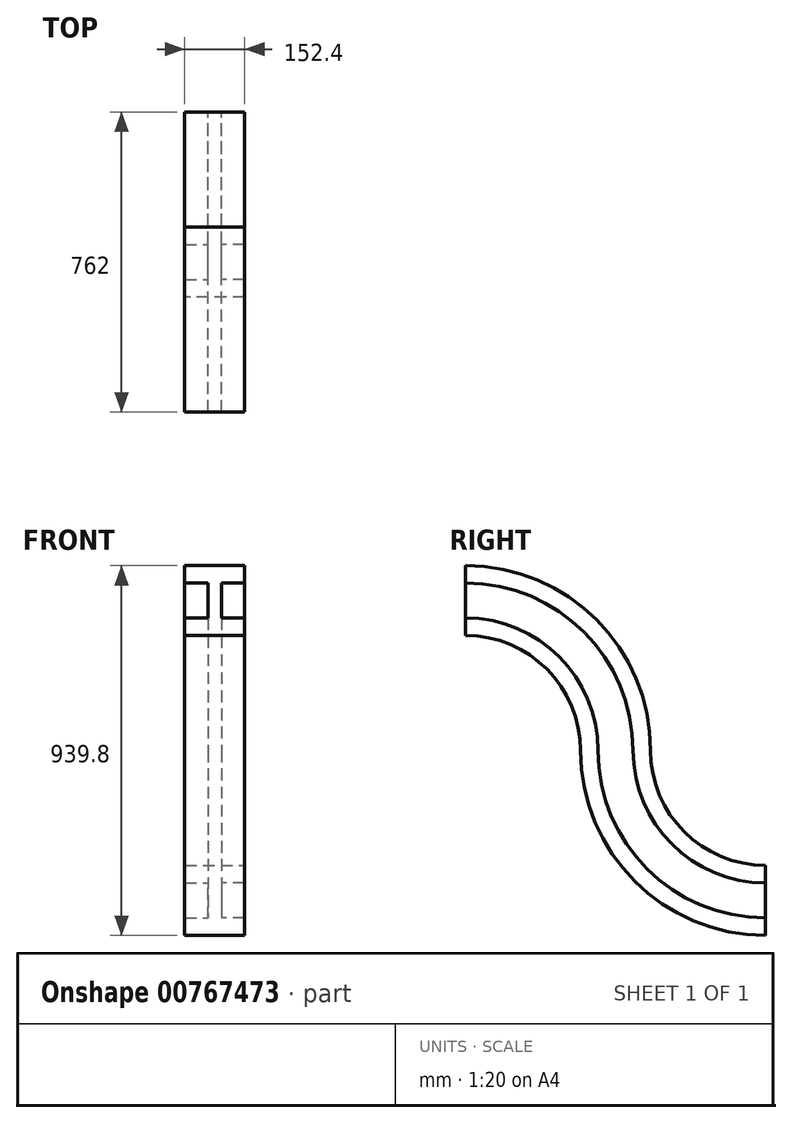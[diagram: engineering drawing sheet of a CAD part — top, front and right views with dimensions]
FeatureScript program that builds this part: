
annotation { "Feature Type Name" : "Feature", "Feature Type Description" : "" }
export const myFeature = defineFeature(function(context is Context, id is Id, definition is map)
    precondition{}
    {
        {
            var Q0;
            Q0=qCreatedBy(makeId("Front.planeOp"),FACE);
            var sketch = newSketch(context, id + "F0", { "sketchPlane" : qUnion([Q0])});
            skLineSegment(sketch, "E0", {"start": v(0, 88.9) * mm, "end": v(76.2, 88.9) * mm});
            skLineSegment(sketch, "E1", {"start": v(76.2, 88.9) * mm, "end": v(76.2, 44.45) * mm});
            skLineSegment(sketch, "E2", {"start": v(76.2, 44.45) * mm, "end": v(17.37, 44.45) * mm});
            skLineSegment(sketch, "E3", {"start": v(0, 88.9) * mm, "end": v(0, -88.9) * mm, "construction": true});
            skLineSegment(sketch, "E4", {"start": v(-17.37, 0) * mm, "end": v(17.37, 0) * mm, "construction": true});
            skLineSegment(sketch, "E5", {"start": v(17.37, 0) * mm, "end": v(17.37, 44.45) * mm});
            skLineSegment(sketch, "E6.MirrorCS", {"start": v(0, 88.9) * mm, "end": v(-76.2, 88.9) * mm});
            skLineSegment(sketch, "E7.MirrorCS", {"start": v(-76.2, 88.9) * mm, "end": v(-76.2, 44.45) * mm});
            skLineSegment(sketch, "E8.MirrorCS", {"start": v(-17.37, 0) * mm, "end": v(-17.37, 44.45) * mm});
            skLineSegment(sketch, "E9.MirrorCS", {"start": v(-76.2, 44.45) * mm, "end": v(-17.37, 44.45) * mm});
            skLineSegment(sketch, "E10.MirrorCS", {"start": v(0, -88.9) * mm, "end": v(-76.2, -88.9) * mm});
            skLineSegment(sketch, "E11.MirrorCS", {"start": v(-76.2, -88.9) * mm, "end": v(-76.2, -44.45) * mm});
            skLineSegment(sketch, "E12.MirrorCS", {"start": v(-76.2, -44.45) * mm, "end": v(-17.37, -44.45) * mm});
            skLineSegment(sketch, "E13.MirrorCS", {"start": v(-17.37, 0) * mm, "end": v(-17.37, -44.45) * mm});
            skLineSegment(sketch, "E14.MirrorCS", {"start": v(76.2, -44.45) * mm, "end": v(17.37, -44.45) * mm});
            skLineSegment(sketch, "E15.MirrorCS", {"start": v(0, -88.9) * mm, "end": v(76.2, -88.9) * mm});
            skLineSegment(sketch, "E16.MirrorCS", {"start": v(17.37, 0) * mm, "end": v(17.37, -44.45) * mm});
            skLineSegment(sketch, "E17.MirrorCS", {"start": v(76.2, -88.9) * mm, "end": v(76.2, -44.45) * mm});
            skSolve(sketch);
        }
        {
            var Q0;
            Q0=qCreatedBy(makeId("Right.planeOp"),FACE);
            var sketch = newSketch(context, id + "F1", { "sketchPlane" : qUnion([Q0])});
            skArc(sketch, "E18", {"start": v(0, 0) * mm, "mid": v(269.4, -111.6) * mm, "end": v(381, -381) * mm});
            skArc(sketch, "E19", {"start": v(381, -381) * mm, "mid": v(492.6, -650.4) * mm, "end": v(762, -762) * mm});
            skSolve(sketch);
        }
        {
            var Q0;
            Q0=qSketchRegion(id+"F0",true);
            var Q1;
            Q1=sQuery(id+"F1.wireOp",EDGE,"E18");
            var Q2;
            Q2=sQuery(id+"F1.wireOp",EDGE,"E19");
            sweep(context, id + "F2", {"profiles" : qUnion([Q0]), "path" : qUnion([Q1, Q2])});
        }
        {
            var Q0;
            Q0=makeQuery(id+"F0.imprint","IMPRINT",FACE,{"disambiguationData":[TD([[makeQuery(id+"F0.imprint","IMPRINT",EDGE,{"derivedFrom":sQuery(id+"F0.wireOp",EDGE,"E0")}),-1.0]])]});
            var Q1;
            Q1=sQuery(id+"F1.wireOp",EDGE,"E18");
            var Q2;
            Q2=sQuery(id+"F1.wireOp",EDGE,"E19");
            sweep(context, id + "F3", {"profiles" : qUnion([Q0]), "path" : qUnion([Q1, Q2])});
        }
    });
